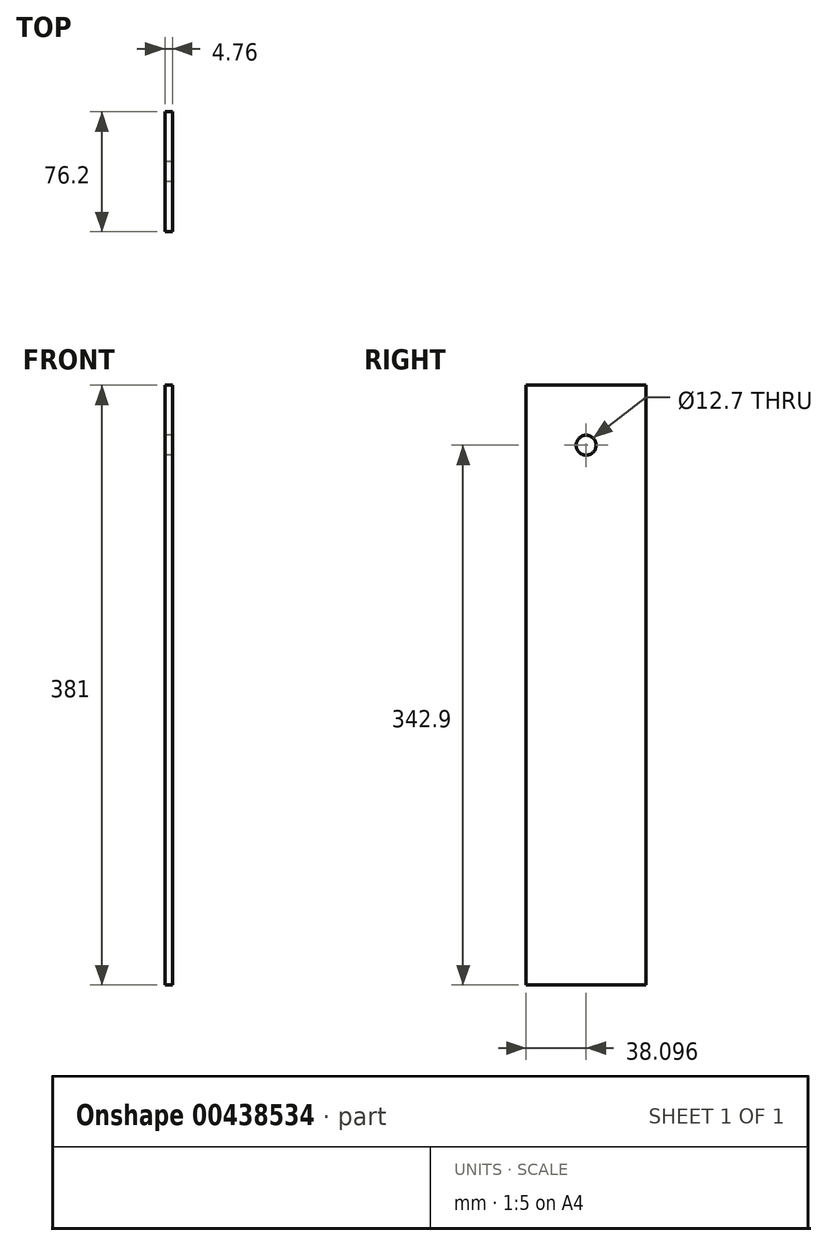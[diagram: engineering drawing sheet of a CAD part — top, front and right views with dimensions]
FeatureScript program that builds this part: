
annotation { "Feature Type Name" : "Feature", "Feature Type Description" : "" }
export const myFeature = defineFeature(function(context is Context, id is Id, definition is map)
    precondition{}
    {
        {
            var Q0;
            Q0=qCreatedBy(makeId("Right.planeOp"),FACE);
            var sketch = newSketch(context, id + "F0", { "sketchPlane" : qUnion([Q0])});
            skLineSegment(sketch, "E0.bottom", {"start": v(-40.57, 332.92) * mm, "end": v(35.63, 332.92) * mm});
            skLineSegment(sketch, "E0.top", {"start": v(-40.57, -48.08) * mm, "end": v(35.63, -48.08) * mm});
            skLineSegment(sketch, "E0.left", {"start": v(-40.57, 332.92) * mm, "end": v(-40.57, -48.08) * mm});
            skLineSegment(sketch, "E0.right", {"start": v(35.63, 332.92) * mm, "end": v(35.63, -48.08) * mm});
            skCircle(sketch, "E1", {"center": v(-2.47, 294.82) * mm, "radius": 6.35 * mm});
            skSolve(sketch);
        }
        {
            var Q0;
            Q0=makeQuery(id+"F0.imprint","IMPRINT",FACE,{"disambiguationData":[TD([[makeQuery(id+"F0.imprint","IMPRINT",EDGE,{"derivedFrom":sQuery(id+"F0.wireOp",EDGE,"E0.bottom")}),-1.0]])]});
            extrude(context, id + "F1", {"entities" : qUnion([Q0]), "depth" : 4.76 * mm});
        }
    });
